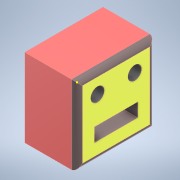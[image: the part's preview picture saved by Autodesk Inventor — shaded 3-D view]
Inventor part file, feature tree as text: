
AUTODESK INVENTOR PART (.ipt)
format: ipt  version: 2022 (Build 260153070, 153G)  size: 163,328 bytes
history: native  units: mm
features: sketch x5, extrude x3, fillet x1
ambient origin geometry x8: Origin, YZ Plane, XZ Plane, XY Plane, X Axis, Y Axis, Z Axis, Center Point
bodies: Solid1 (feature_tree)
feature tree (9):
  extrude  "Extrusion1"  Depth=114.3mm
  extrude  "Extrusion2"  Depth=20.0mm
  sketch  "Sketch3"  dims[d6=63.5mm d7=20.0mm]
  fillet  "Fillet2"  Radius=20.0mm
  sketch  "Sketch4"  dims[d8=30.0mm]
  extrude  "Extrusion3"  Depth=20.0mm
  sketch  "Sketch1"  dims[d0=114.3mm d1=114.3mm]
  sketch  "Sketch2"  dims[d2=76.2mm d3=0.0mm d4=20.0mm d5=20.0mm]
  sketch  "Sketch5"  dims[d9=30.0mm d10=30.0mm d11=30.0mm d12=25.4mm d13=25.4mm d14=0.0mm d15=0.0mm d17=8.0mm d18=4.0mm d19=4.0mm d20=25.4mm d21=12.7mm d22=57.15mm d23=57.15mm d24=25.4mm d25=0.0mm]
